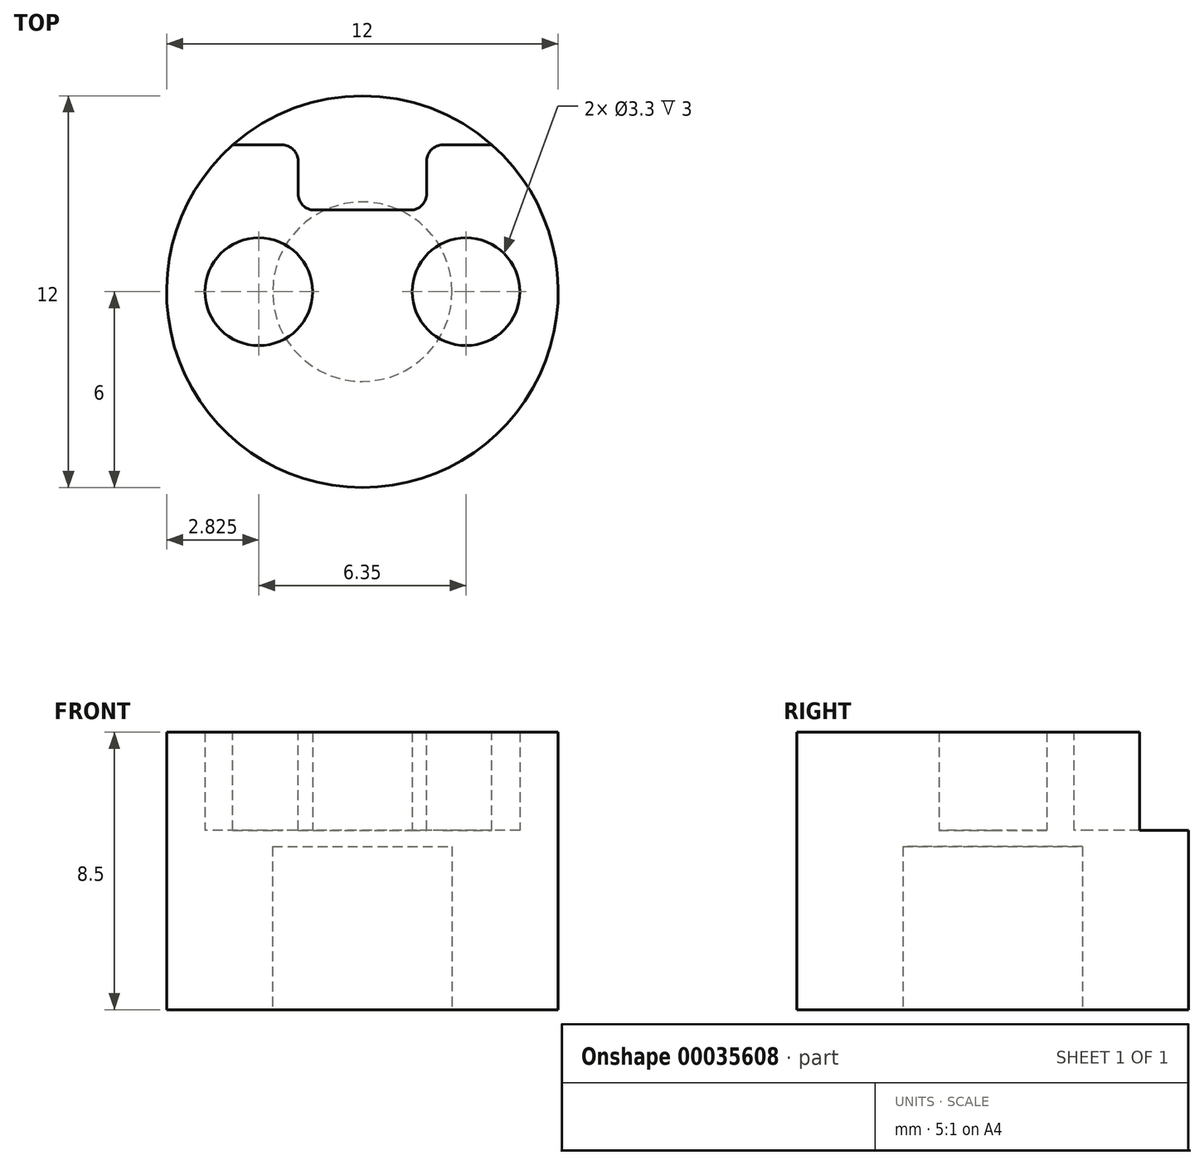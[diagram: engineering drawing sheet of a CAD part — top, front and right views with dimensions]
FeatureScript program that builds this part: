
annotation { "Feature Type Name" : "Feature", "Feature Type Description" : "" }
export const myFeature = defineFeature(function(context is Context, id is Id, definition is map)
    precondition{}
    {
        {
            var Q0;
            Q0=qCreatedBy(makeId("Top.planeOp"),FACE);
            var sketch = newSketch(context, id + "F0", { "sketchPlane" : qUnion([Q0])});
            skCircle(sketch, "E0", {"center": v(-3.18, 0) * mm, "radius": 1.65 * mm});
            skCircle(sketch, "E1", {"center": v(3.18, 0) * mm, "radius": 1.65 * mm});
            skCircle(sketch, "E2", {"center": v(0, 0) * mm, "radius": 6 * mm});
            skSolve(sketch);
        }
        {
            var Q0;
            Q0 = qSketchRegion(id + "F0", true);
            extrude(context, id + "F1", {"entities" : qUnion([Q0]), "depth" : 3 * mm});
        }
        {
            var Q0;
            Q0=makeQuery(id+"F1.opExtrude","CAP_FACE",FACE,{"disambiguationData":[OSD([sQuery(id+"F0.wireOp",EDGE,"E0"),sQuery(id+"F0.wireOp",EDGE,"E1"),sQuery(id+"F0.wireOp",EDGE,"E2"),sQuery(id+"F0.wireOp",EDGE,"mxWlrIbW-bbLS-1jjZ-dLkJ-aSx3uFq2Umk3")])],"isStart":true});
            var sketch = newSketch(context, id + "F2", { "sketchPlane" : qUnion([Q0])});
            skCircle(sketch, "E3.0", {"center": v(0, 0) * mm, "radius": 6 * mm});
            skSolve(sketch);
        }
        {
            var Q0;
            Q0 = qSketchRegion(id + "F2", true);
            extrude(context, id + "F3", {"entities" : qUnion([Q0]), "operationType" : NewBodyOperationType.ADD, "depth" : 5.5 * mm});
        }
        {
            var Q0;
            Q0=makeQuery(id+"F1.opExtrude","CAP_FACE",FACE,{"disambiguationData":[OSD([sQuery(id+"F0.wireOp",EDGE,"E0"),sQuery(id+"F0.wireOp",EDGE,"E1"),sQuery(id+"F0.wireOp",EDGE,"E2"),sQuery(id+"F0.wireOp",EDGE,"mxWlrIbW-bbLS-1jjZ-dLkJ-aSx3uFq2Umk3")])],"isStart":false});
            var sketch = newSketch(context, id + "F4", { "sketchPlane" : qUnion([Q0])});
            skLineSegment(sketch, "E4", {"start": v(-3.97, 4.5) * mm, "end": v(-1.97, 4.5) * mm});
            skLineSegment(sketch, "E5", {"start": v(-1.97, 4.5) * mm, "end": v(-1.97, 2.5) * mm});
            skLineSegment(sketch, "E6", {"start": v(-1.97, 2.5) * mm, "end": v(1.97, 2.5) * mm});
            skLineSegment(sketch, "E7", {"start": v(1.97, 2.5) * mm, "end": v(1.97, 4.5) * mm});
            skLineSegment(sketch, "E8", {"start": v(1.97, 4.5) * mm, "end": v(3.97, 4.5) * mm});
            skCircle(sketch, "E9.0", {"center": v(0, 0) * mm, "radius": 6 * mm});
            skSolve(sketch);
        }
        {
            var Q0;
            {var subQ1=sQuery(id+"F4.wireOp",EDGE,"E4");Q0=makeQuery(id+"F4.imprint","IMPRINT",FACE,{"disambiguationData":[TD([[makeQuery(id+"F4.imprint","IMPRINT",EDGE,{"derivedFrom":subQ1}),1.0]])]});}
            extrude(context, id + "F5", {"entities" : qUnion([Q0]), "operationType" : NewBodyOperationType.REMOVE, "oppositeDirection" : true, "depth" : 3 * mm});
        }
        {
            var Q0;
            Q0=makeQuery(id+"F5.boolean.opBoolean","COPY",EDGE,{"derivedFrom":makeQuery(id+"F5.opExtrude","SWEPT_EDGE",EDGE,{"disambiguationData":[OSD([sQuery(id+"F4.wireOp",EDGE,"E4"),sQuery(id+"F4.wireOp",EDGE,"E9.0")])]})});
            var Q1;
            Q1=makeQuery(id+"F5.boolean.opBoolean","COPY",EDGE,{"derivedFrom":makeQuery(id+"F5.opExtrude","SWEPT_EDGE",EDGE,{"disambiguationData":[OSD([sQuery(id+"F4.wireOp",EDGE,"E4"),sQuery(id+"F4.wireOp",EDGE,"E5")])]})});
            var Q2;
            Q2=makeQuery(id+"F5.boolean.opBoolean","COPY",EDGE,{"derivedFrom":makeQuery(id+"F5.opExtrude","SWEPT_EDGE",EDGE,{"disambiguationData":[OSD([sQuery(id+"F4.wireOp",EDGE,"E6"),sQuery(id+"F4.wireOp",EDGE,"E7")])]})});
            var Q3;
            Q3=makeQuery(id+"F5.boolean.opBoolean","COPY",EDGE,{"derivedFrom":makeQuery(id+"F5.opExtrude","SWEPT_EDGE",EDGE,{"disambiguationData":[OSD([sQuery(id+"F4.wireOp",EDGE,"E7"),sQuery(id+"F4.wireOp",EDGE,"E8")])]})});
            var Q4;
            Q4=makeQuery(id+"F5.boolean.opBoolean","COPY",EDGE,{"derivedFrom":makeQuery(id+"F5.opExtrude","SWEPT_EDGE",EDGE,{"disambiguationData":[OSD([sQuery(id+"F4.wireOp",EDGE,"E8"),sQuery(id+"F4.wireOp",EDGE,"E9.0")])]})});
            var Q5;
            Q5=makeQuery(id+"F5.boolean.opBoolean","COPY",EDGE,{"derivedFrom":makeQuery(id+"F5.opExtrude","SWEPT_EDGE",EDGE,{"disambiguationData":[OSD([sQuery(id+"F4.wireOp",EDGE,"E5"),sQuery(id+"F4.wireOp",EDGE,"E6")])]})});
            fillet(context, id + "F6", {"entities" : qUnion([Q0, Q1, Q2, Q3, Q4, Q5]), "radius" : .5 * mm, "tangentPropagation" : true, "allowEdgeOverflow" : false});
        }
        {
            var Q0;
            Q0=makeQuery(id+"F3.opExtrude","CAP_FACE",FACE,{"disambiguationData":[OSD([sQuery(id+"F2.wireOp",EDGE,"E3.0")])],"isStart":false});
            var sketch = newSketch(context, id + "F7", { "sketchPlane" : qUnion([Q0])});
            skCircle(sketch, "E10", {"center": v(0, 0) * mm, "radius": 2.75 * mm});
            skSolve(sketch);
        }
        {
            var Q0;
            Q0 = qSketchRegion(id + "F7", true);
            extrude(context, id + "F8", {"entities" : qUnion([Q0]), "operationType" : NewBodyOperationType.REMOVE, "oppositeDirection" : true, "depth" : 5 * mm});
        }
    });
